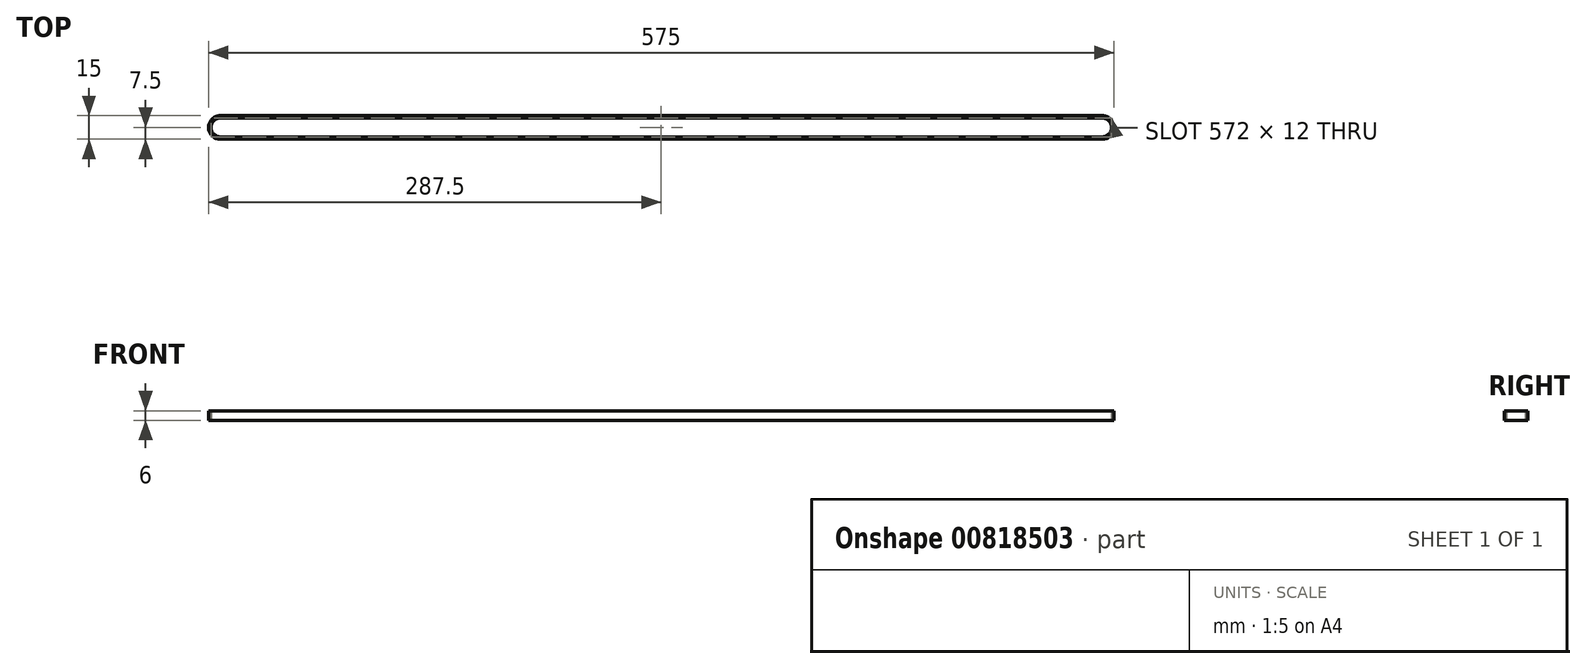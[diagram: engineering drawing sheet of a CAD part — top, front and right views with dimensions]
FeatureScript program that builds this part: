
annotation { "Feature Type Name" : "Feature", "Feature Type Description" : "" }
export const myFeature = defineFeature(function(context is Context, id is Id, definition is map)
    precondition{}
    {
        {
            var Q0;
            Q0=qCreatedBy(makeId("Top.planeOp"),FACE);
            var sketch = newSketch(context, id + "F0", { "sketchPlane" : qUnion([Q0])});
            skLineSegment(sketch, "E0", {"start": v(-280, 0) * mm, "end": v(280, 0) * mm, "construction": true});
            skArc(sketch, "E1.0.startCap", {"start": v(-280, -6) * mm, "mid": v(-286, 0) * mm, "end": v(-280, 6) * mm});
            skArc(sketch, "E1.0.endCap", {"start": v(280, 6) * mm, "mid": v(286, 0) * mm, "end": v(280, -6) * mm});
            skLineSegment(sketch, "E1.0.left", {"start": v(-280, 6) * mm, "end": v(280, 6) * mm});
            skLineSegment(sketch, "E1.0.right", {"start": v(-280, -6) * mm, "end": v(280, -6) * mm});
            skArc(sketch, "E2.0.startCap", {"start": v(-280, -7.5) * mm, "mid": v(-287.5, 0) * mm, "end": v(-280, 7.5) * mm});
            skArc(sketch, "E2.0.endCap", {"start": v(280, 7.5) * mm, "mid": v(287.5, 0) * mm, "end": v(280, -7.5) * mm});
            skLineSegment(sketch, "E2.0.left", {"start": v(-280, 7.5) * mm, "end": v(280, 7.5) * mm});
            skLineSegment(sketch, "E2.0.right", {"start": v(-280, -7.5) * mm, "end": v(280, -7.5) * mm});
            skSolve(sketch);
        }
        {
            var Q0;
            Q0=qSketchRegion(id+"F0",true);
            extrude(context, id + "F1", {"entities" : qUnion([Q0]), "endBound" : BoundingType.SYMMETRIC, "depth" : 6 * mm});
        }
    });
